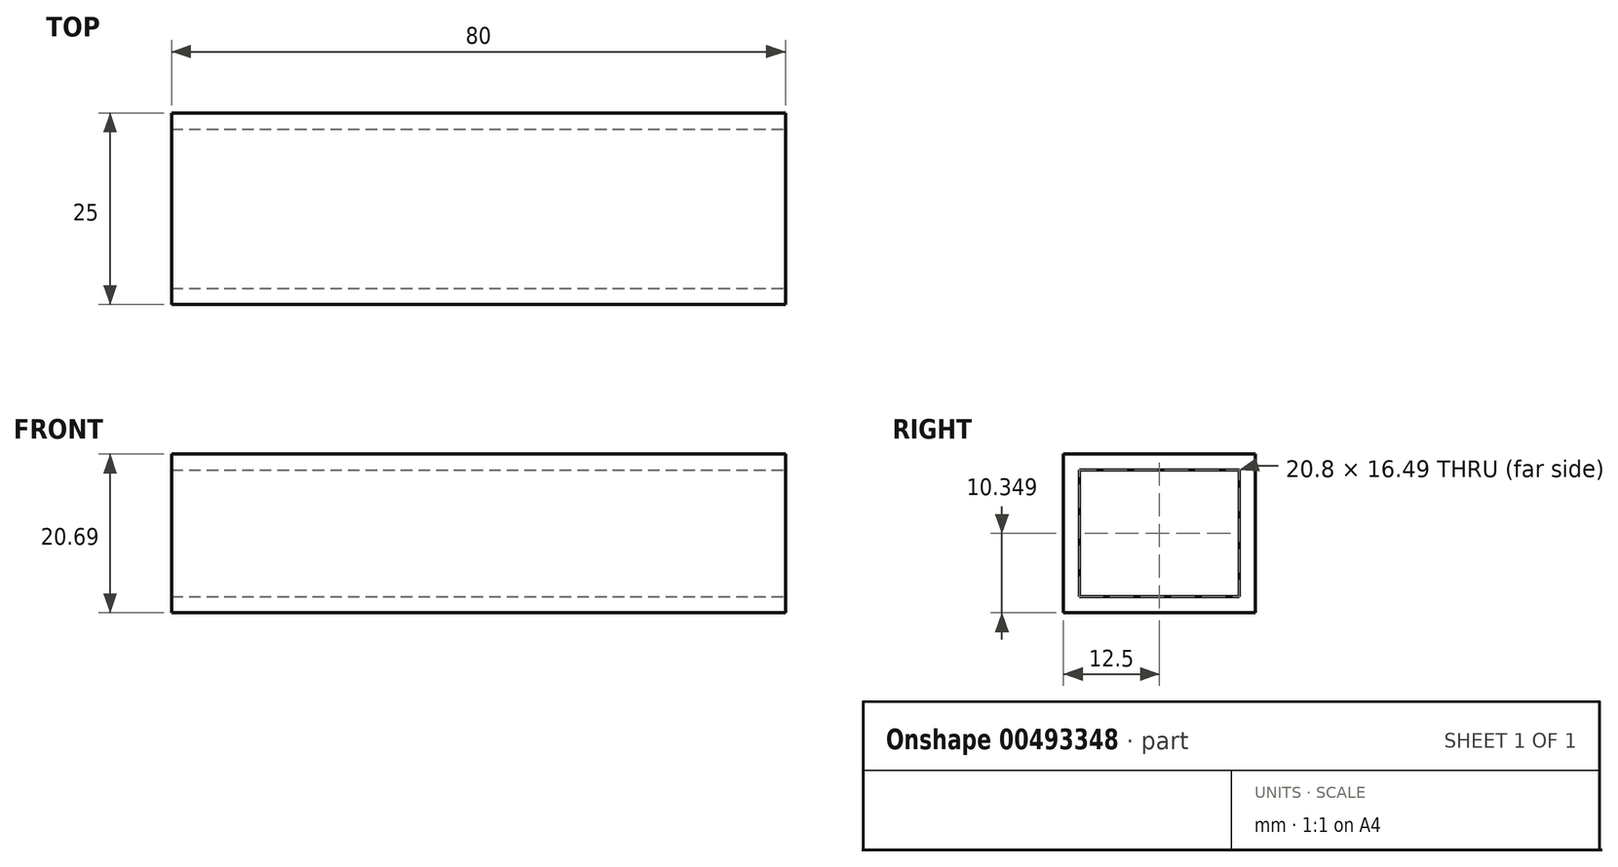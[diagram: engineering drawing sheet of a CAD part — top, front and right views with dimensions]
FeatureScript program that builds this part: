
annotation { "Feature Type Name" : "Feature", "Feature Type Description" : "" }
export const myFeature = defineFeature(function(context is Context, id is Id, definition is map)
    precondition{}
    {
        {
            var Q0;
            Q0=qCreatedBy(makeId("Front.planeOp"),FACE);
            var sketch = newSketch(context, id + "F0", { "sketchPlane" : qUnion([Q0])});
            skLineSegment(sketch, "E0.bottom", {"start": v(-69.26, -37.86) * mm, "end": v(10.74, -37.86) * mm});
            skLineSegment(sketch, "E0.top", {"start": v(-69.26, -58.55) * mm, "end": v(10.74, -58.55) * mm});
            skLineSegment(sketch, "E0.left", {"start": v(-69.26, -37.86) * mm, "end": v(-69.26, -58.55) * mm});
            skLineSegment(sketch, "E0.right", {"start": v(10.74, -37.86) * mm, "end": v(10.74, -58.55) * mm});
            skSolve(sketch);
        }
        {
            var Q0;
            Q0=makeQuery(id+"F0.imprint","IMPRINT",FACE,{"disambiguationData":[TD([[makeQuery(id+"F0.imprint","IMPRINT",EDGE,{"derivedFrom":sQuery(id+"F0.wireOp",EDGE,"E0.bottom")}),-1.0]])]});
            extrude(context, id + "F1", {"entities" : qUnion([Q0]), "oppositeDirection" : true, "depth" : 25 * mm});
        }
        {
            var Q0;
            Q0=makeQuery(id+"F1.opExtrude","SWEPT_FACE",FACE,{"disambiguationData":[OSD([sQuery(id+"F0.wireOp",EDGE,"E0.right")])]});
            var Q1;
            Q1=makeQuery(id+"F1.opExtrude","SWEPT_FACE",FACE,{"disambiguationData":[OSD([sQuery(id+"F0.wireOp",EDGE,"E0.left")])]});
            shell(context, id + "F2", {"entities" : qUnion([Q0, Q1]), "thickness" : 2.1 * mm});
        }
    });
